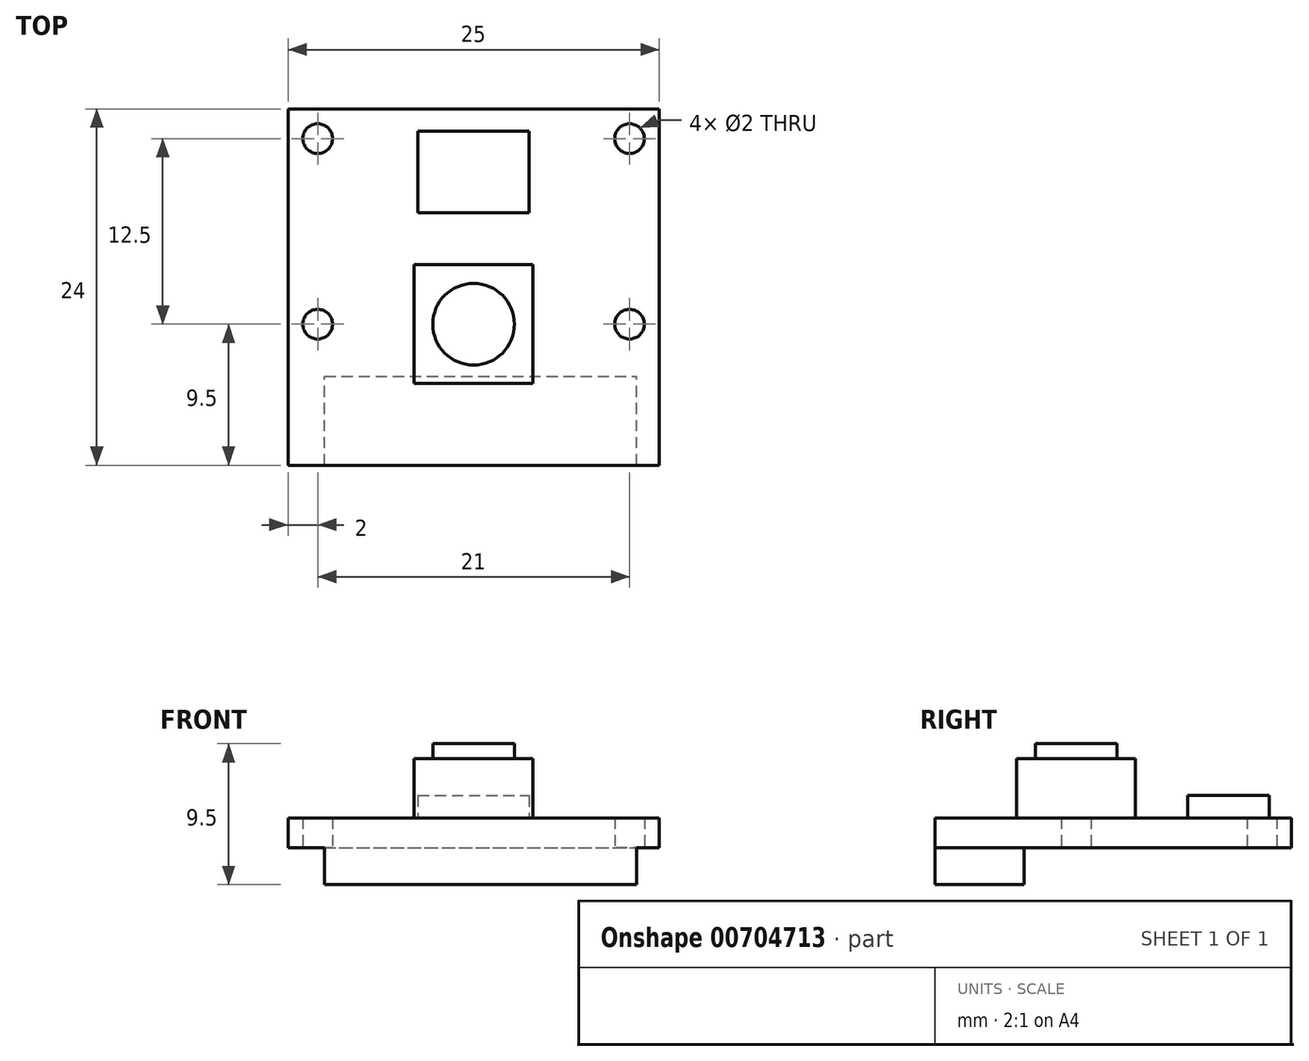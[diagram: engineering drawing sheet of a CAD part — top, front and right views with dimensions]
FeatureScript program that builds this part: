
annotation { "Feature Type Name" : "Feature", "Feature Type Description" : "" }
export const myFeature = defineFeature(function(context is Context, id is Id, definition is map)
    precondition{}
    {
        {
            var Q0;
            Q0=qCreatedBy(makeId("Top.planeOp"),FACE);
            var sketch = newSketch(context, id + "F0", { "sketchPlane" : qUnion([Q0])});
            skLineSegment(sketch, "E0.bottom", {"start": v(-12.5, 12) * mm, "end": v(12.5, 12) * mm});
            skLineSegment(sketch, "E0.top", {"start": v(-12.5, -12) * mm, "end": v(12.5, -12) * mm});
            skLineSegment(sketch, "E0.left", {"start": v(-12.5, 12) * mm, "end": v(-12.5, -12) * mm});
            skLineSegment(sketch, "E0.right", {"start": v(12.5, 12) * mm, "end": v(12.5, -12) * mm});
            skLineSegment(sketch, "E1.bottom", {"start": v(-4, 1.5) * mm, "end": v(4, 1.5) * mm});
            skLineSegment(sketch, "E1.top", {"start": v(-4, -6.5) * mm, "end": v(4, -6.5) * mm});
            skLineSegment(sketch, "E1.left", {"start": v(-4, 1.5) * mm, "end": v(-4, -6.5) * mm});
            skLineSegment(sketch, "E1.right", {"start": v(4, 1.5) * mm, "end": v(4, -6.5) * mm});
            skCircle(sketch, "E2", {"center": v(10.5, 10) * mm, "radius": 1 * mm});
            skCircle(sketch, "E3", {"center": v(-10.5, 10) * mm, "radius": 1 * mm});
            skCircle(sketch, "E4", {"center": v(10.5, -2.5) * mm, "radius": 1 * mm});
            skCircle(sketch, "E5", {"center": v(-10.5, -2.5) * mm, "radius": 1 * mm});
            skCircle(sketch, "E6", {"center": v(0, -2.5) * mm, "radius": 2.75 * mm});
            skLineSegment(sketch, "E7.bottom", {"start": v(-10.04, -12) * mm, "end": v(10.96, -12) * mm});
            skLineSegment(sketch, "E7.top", {"start": v(-10.04, -6) * mm, "end": v(10.96, -6) * mm});
            skLineSegment(sketch, "E7.left", {"start": v(-10.04, -12) * mm, "end": v(-10.04, -6) * mm});
            skLineSegment(sketch, "E7.right", {"start": v(10.96, -12) * mm, "end": v(10.96, -6) * mm});
            skLineSegment(sketch, "E8.bottom", {"start": v(-3.75, 10.5) * mm, "end": v(3.75, 10.5) * mm});
            skLineSegment(sketch, "E8.top", {"start": v(-3.75, 5) * mm, "end": v(3.75, 5) * mm});
            skLineSegment(sketch, "E8.left", {"start": v(-3.75, 10.5) * mm, "end": v(-3.75, 5) * mm});
            skLineSegment(sketch, "E8.right", {"start": v(3.75, 10.5) * mm, "end": v(3.75, 5) * mm});
            skSolve(sketch);
        }
        {
            var Q0;
            {var subQ1=sQuery(id+"F0.wireOp",EDGE,"E1.top");Q0=makeQuery(id+"F0.imprint","IMPRINT",FACE,{"disambiguationData":[TD([[makeQuery(id+"F0.imprint","IMPRINT",EDGE,{"derivedFrom":subQ1}),-1.0]])]});}
            var Q1;
            Q1=makeQuery(id+"F0.imprint","IMPRINT",FACE,{"disambiguationData":[TD([[makeQuery(id+"F0.imprint","IMPRINT",EDGE,{"derivedFrom":sQuery(id+"F0.wireOp",EDGE,"E0.bottom")}),-1.0]])]});
            var Q2;
            Q2=makeQuery(id+"F0.imprint","IMPRINT",FACE,{"disambiguationData":[TD([[makeQuery(id+"F0.imprint","IMPRINT",EDGE,{"derivedFrom":sQuery(id+"F0.wireOp",EDGE,"E8.bottom")}),-1.0]])]});
            var Q3;
            {var subQ1=sQuery(id+"F0.wireOp",EDGE,"E1.bottom");Q3=makeQuery(id+"F0.imprint","IMPRINT",FACE,{"disambiguationData":[TD([[makeQuery(id+"F0.imprint","IMPRINT",EDGE,{"derivedFrom":subQ1}),-1.0]])]});}
            var Q4;
            Q4=makeQuery(id+"F0.imprint","IMPRINT",FACE,{"disambiguationData":[TD([[makeQuery(id+"F0.imprint","IMPRINT",EDGE,{"derivedFrom":sQuery(id+"F0.wireOp",EDGE,"E6")}),1.0]])]});
            var Q5;
            {var subQ0=sQuery(id+"F0.wireOp",EDGE,"E1.top");Q5=makeQuery(id+"F0.imprint","IMPRINT",FACE,{"disambiguationData":[TD([[makeQuery(id+"F0.imprint","IMPRINT",EDGE,{"derivedFrom":subQ0}),1.0]])]});}
            extrude(context, id + "F1", {"entities" : qUnion([Q0, Q1, Q2, Q3, Q4, Q5]), "depth" : 2 * mm, "offsetDistance" : 25 * mm, "symmetric" : true});
        }
        {
            var Q0;
            {var subQ1=sQuery(id+"F0.wireOp",EDGE,"E1.top");Q0=makeQuery(id+"F0.imprint","IMPRINT",FACE,{"disambiguationData":[TD([[makeQuery(id+"F0.imprint","IMPRINT",EDGE,{"derivedFrom":subQ1}),-1.0]])]});}
            var Q1;
            {var subQ0=sQuery(id+"F0.wireOp",EDGE,"E1.top");Q1=makeQuery(id+"F0.imprint","IMPRINT",FACE,{"disambiguationData":[TD([[makeQuery(id+"F0.imprint","IMPRINT",EDGE,{"derivedFrom":subQ0}),1.0]])]});}
            extrude(context, id + "F2", {"entities" : qUnion([Q0, Q1]), "operationType" : NewBodyOperationType.ADD, "oppositeDirection" : true, "depth" : 3.5 * mm, "offsetDistance" : 25 * mm});
        }
        {
            var Q0;
            {var subQ1=sQuery(id+"F0.wireOp",EDGE,"E1.bottom");Q0=makeQuery(id+"F0.imprint","IMPRINT",FACE,{"disambiguationData":[TD([[makeQuery(id+"F0.imprint","IMPRINT",EDGE,{"derivedFrom":subQ1}),-1.0]])]});}
            var Q1;
            Q1=makeQuery(id+"F0.imprint","IMPRINT",FACE,{"disambiguationData":[TD([[makeQuery(id+"F0.imprint","IMPRINT",EDGE,{"derivedFrom":sQuery(id+"F0.wireOp",EDGE,"E6")}),1.0]])]});
            var Q2;
            {var subQ0=sQuery(id+"F0.wireOp",EDGE,"E1.top");Q2=makeQuery(id+"F0.imprint","IMPRINT",FACE,{"disambiguationData":[TD([[makeQuery(id+"F0.imprint","IMPRINT",EDGE,{"derivedFrom":subQ0}),1.0]])]});}
            extrude(context, id + "F3", {"entities" : qUnion([Q0, Q1, Q2]), "operationType" : NewBodyOperationType.ADD, "depth" : 5 * mm, "offsetDistance" : 25 * mm});
        }
        {
            var Q0;
            Q0=makeQuery(id+"F0.imprint","IMPRINT",FACE,{"disambiguationData":[TD([[makeQuery(id+"F0.imprint","IMPRINT",EDGE,{"derivedFrom":sQuery(id+"F0.wireOp",EDGE,"E6")}),1.0]])]});
            extrude(context, id + "F4", {"entities" : qUnion([Q0]), "operationType" : NewBodyOperationType.ADD, "depth" : 6 * mm, "offsetDistance" : 25 * mm});
        }
        {
            var Q0;
            Q0=makeQuery(id+"F0.imprint","IMPRINT",FACE,{"disambiguationData":[TD([[makeQuery(id+"F0.imprint","IMPRINT",EDGE,{"derivedFrom":sQuery(id+"F0.wireOp",EDGE,"E8.bottom")}),-1.0]])]});
            extrude(context, id + "F5", {"entities" : qUnion([Q0]), "operationType" : NewBodyOperationType.ADD, "depth" : 2.5 * mm, "offsetDistance" : 25 * mm});
        }
    });
